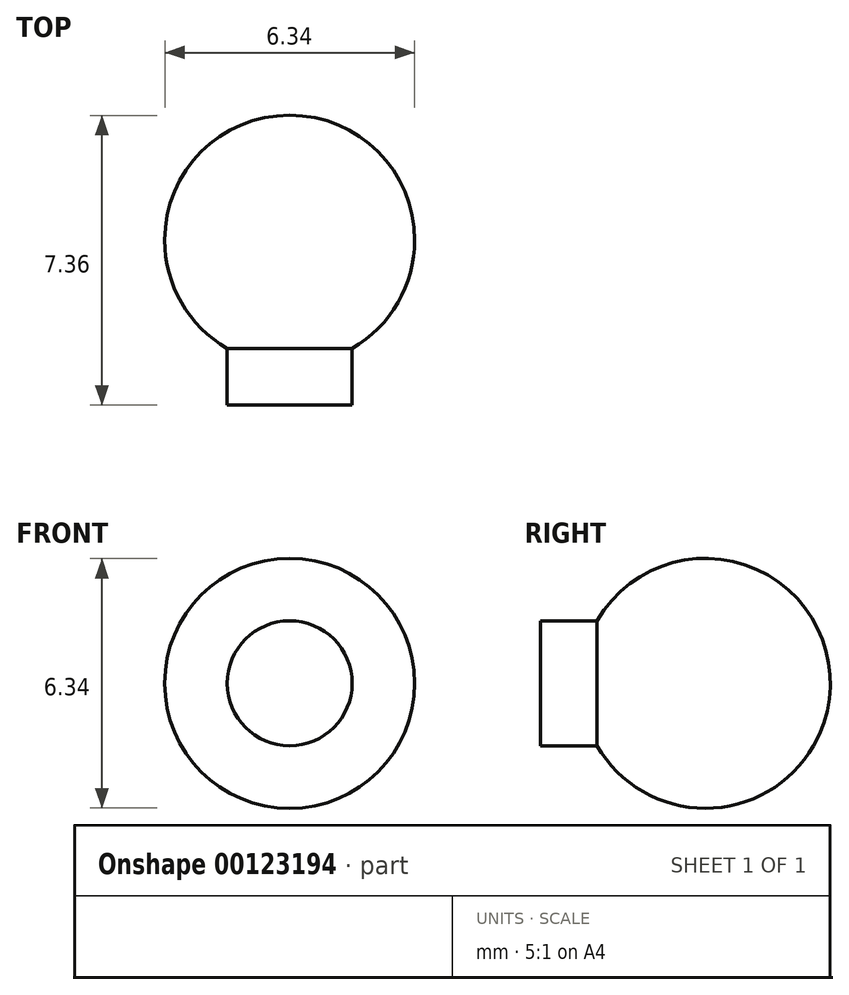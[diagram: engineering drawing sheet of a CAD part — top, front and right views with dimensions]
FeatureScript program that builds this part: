
annotation { "Feature Type Name" : "Feature", "Feature Type Description" : "" }
export const myFeature = defineFeature(function(context is Context, id is Id, definition is map)
    precondition{}
    {
        {
            var Q0;
            Q0=qCreatedBy(makeId("Front.planeOp"),FACE);
            var sketch = newSketch(context, id + "F0", { "sketchPlane" : qUnion([Q0])});
            skArc(sketch, "E0", {"start": v(-3.18, 0) * mm, "mid": v(0, -3.18) * mm, "end": v(3.18, 0) * mm});
            skLineSegment(sketch, "E1", {"start": v(3.18, 0) * mm, "end": v(-3.18, 0) * mm});
            skSolve(sketch);
        }
        {
            var Q0;
            Q0=makeQuery(id+"F0.imprint","IMPRINT",FACE,{"disambiguationData":[TD([[makeQuery(id+"F0.imprint","IMPRINT",EDGE,{"derivedFrom":sQuery(id+"F0.wireOp",EDGE,"E0")}),1.0]])]});
            var Q1;
            Q1=sQuery(id+"F0.wireOp",EDGE,"E1");
            revolve(context, id + "F1", {"entities" : qUnion([Q0]), "axis" : qUnion([Q1]), "revolveType" : RevolveType.FULL});
        }
        {
            var Q0;
            Q0=qCreatedBy(makeId("Front.planeOp"),FACE);
            var sketch = newSketch(context, id + "F2", { "sketchPlane" : qUnion([Q0])});
            skCircle(sketch, "E2", {"center": v(0, 0) * mm, "radius": 1.59 * mm});
            skSolve(sketch);
        }
        {
            var Q0;
            Q0 = qSketchRegion(id + "F2", true);
            extrude(context, id + "F3", {"entities" : qUnion([Q0]), "operationType" : NewBodyOperationType.ADD, "depth" : 4.2 * mm});
        }
    });
